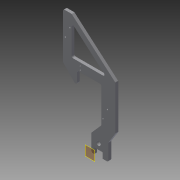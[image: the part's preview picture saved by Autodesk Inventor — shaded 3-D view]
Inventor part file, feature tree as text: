
AUTODESK INVENTOR PART (.ipt)
format: ipt  version: 2013 (Build 170138000, 138)  size: 193,024 bytes
history: native  units: in
note: dims shown in document units (in); Inventor stores cm internally (conversion verified against a paired STEP export)
features: sketch x4, extrude x4, plane x2, fillet x1
ambient origin geometry x8: Origin, YZ Plane, XZ Plane, XY Plane, X Axis, Y Axis, Z Axis, Center Point
bodies: Solid1 (feature_tree)
feature tree (11):
  sketch  "Sketch1"  dims[d0=0.25in d1=0.5in d2=0.75in d3=0.25in d5=0.3765in d6=0.5in d7=0.375in d11=1.25in d23=1.0in]
  plane  "Work Plane1"
  plane  "Work Plane2"
  extrude  "Extrusion6"  Depth=1.0in
  extrude  "Extrusion7"  Depth=1.0in
  fillet  "Fillet3"  Radius=1.5in
  extrude  "Extrusion8"  Depth=0.25in
  extrude  "Extrusion9"  Depth=1.5in
  sketch  "Sketch5"  dims[d24=1.5in d25=1.0in d26=1.5in]
  sketch  "Sketch6"  dims[d27=2.15in d32=0.25in]
  sketch  "Sketch7"  dims[d33=0.875in d34=1.5in d36=3.125in d59=4.8333in d60=4.625in d61=4.0833in d62=0.75in d64=1.25in d66=1.225in d88=0.5in d89=0.2797in d91=0.75in d92=0.75in d93=0.25in d94=0.0in d95=0.15in d96=0.15in d97=1.113in d98=2.019in d99=0.175in d100=0.573in d101=0.375in d102=0.0in d103=0.125in d104=0.125in d105=0.125in d106=0.1875in d107=0.25in d108=0.375in d109=0.0in d110=1.5in d111=1.5in d112=1.5in d113=0.15in d114=0.15in d115=0.906in d116=0.398in d117=0.125in d118=0.125in d119=0.375in d120=0.0in]
